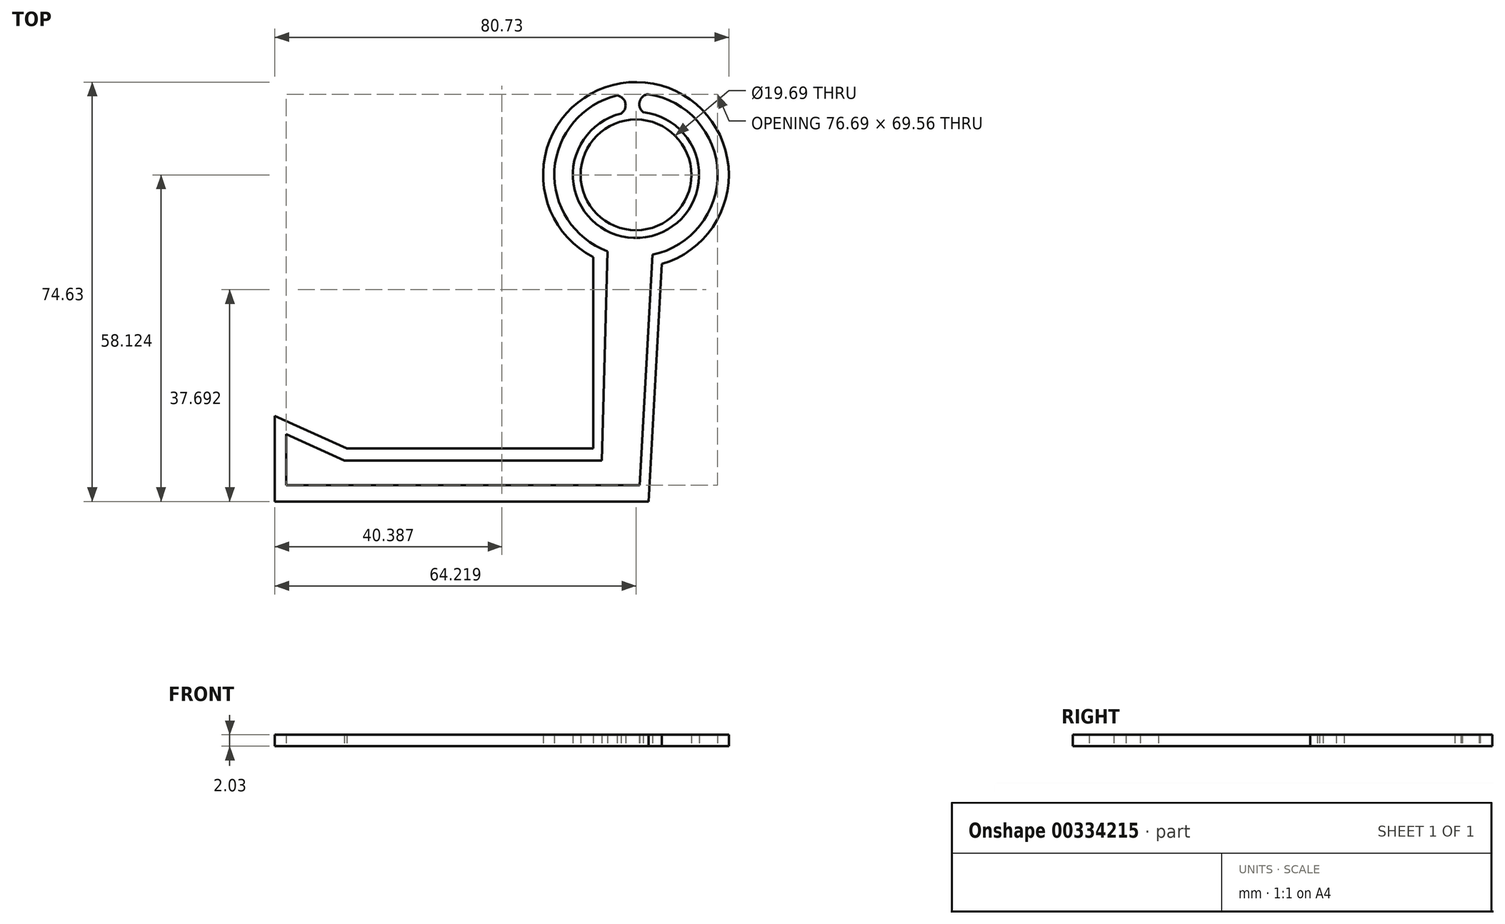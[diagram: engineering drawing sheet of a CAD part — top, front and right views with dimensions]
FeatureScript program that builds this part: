
annotation { "Feature Type Name" : "Feature", "Feature Type Description" : "" }
export const myFeature = defineFeature(function(context is Context, id is Id, definition is map)
    precondition{}
    {
        {
            var Q0;
            Q0=qCreatedBy(makeId("Top.planeOp"),FACE);
            var sketch = newSketch(context, id + "F0", { "sketchPlane" : qUnion([Q0])});
            skArc(sketch, "E0", {"start": v(33.46, 10.72) * mm, "mid": v(30.49, 43) * mm, "end": v(21.23, 11.93) * mm});
            skLineSegment(sketch, "E1", {"start": v(21.23, 11.93) * mm, "end": v(21.23, -22.1) * mm});
            skLineSegment(sketch, "E2", {"start": v(21.23, -22.1) * mm, "end": v(-22.56, -22.1) * mm});
            skLineSegment(sketch, "E3", {"start": v(-22.56, -22.1) * mm, "end": v(-35.36, -16.3) * mm});
            skLineSegment(sketch, "E4", {"start": v(-35.36, -16.3) * mm, "end": v(-35.36, -31.55) * mm});
            skLineSegment(sketch, "E5", {"start": v(-35.36, -31.55) * mm, "end": v(31.09, -31.55) * mm});
            skLineSegment(sketch, "E6", {"start": v(31.09, -31.55) * mm, "end": v(33.46, 10.72) * mm});
            skArc(sketch, "E7", {"start": v(31.82, 12.36) * mm, "mid": v(43.37, 26.96) * mm, "end": v(31.06, 40.92) * mm});
            skLineSegment(sketch, "E8", {"start": v(23.78, 12.97) * mm, "end": v(22.78, -24.23) * mm});
            skLineSegment(sketch, "E9", {"start": v(22.78, -24.23) * mm, "end": v(-23.01, -24.23) * mm});
            skLineSegment(sketch, "E10", {"start": v(-23.01, -24.23) * mm, "end": v(-33.32, -19.56) * mm});
            skLineSegment(sketch, "E11", {"start": v(-33.32, -19.56) * mm, "end": v(-33.32, -28.64) * mm});
            skLineSegment(sketch, "E12", {"start": v(-33.32, -28.64) * mm, "end": v(29.51, -28.64) * mm});
            skLineSegment(sketch, "E13", {"start": v(29.51, -28.64) * mm, "end": v(31.82, 12.36) * mm});
            skArc(sketch, "E14", {"start": v(26.23, 37.5) * mm, "mid": v(29.53, 15.36) * mm, "end": v(30.16, 37.73) * mm});
            skCircle(sketch, "E15", {"center": v(28.86, 26.57) * mm, "radius": 9.84 * mm});
            skArc(sketch, "E16.trimOffspring", {"start": v(25.5, 40.7) * mm, "mid": v(14.37, 27.47) * mm, "end": v(23.78, 12.97) * mm});
            skLineSegment(sketch, "E17.MirrorCS", {"start": v(-171.58, 37.8) * mm, "end": v(-171.58, 37.72) * mm});
            skArc(sketch, "E18", {"start": v(26.23, 37.5) * mm, "mid": v(26.96, 39.35) * mm, "end": v(25.5, 40.7) * mm});
            skArc(sketch, "E19", {"start": v(31.06, 40.92) * mm, "mid": v(29.52, 39.64) * mm, "end": v(30.16, 37.73) * mm});
            skPoint(sketch, "E20.orphan", {"position": v(27.47, 37.72) * mm});
            skPoint(sketch, "E21.end.orphan", {"position": v(28.93, 37.72) * mm});
            skSolve(sketch);
        }
        {
            var Q0;
            Q0 = qSketchRegion(id + "F0", true);
            extrude(context, id + "F1", {"entities" : qUnion([Q0]), "depth" : 2.03 * mm});
        }
    });
